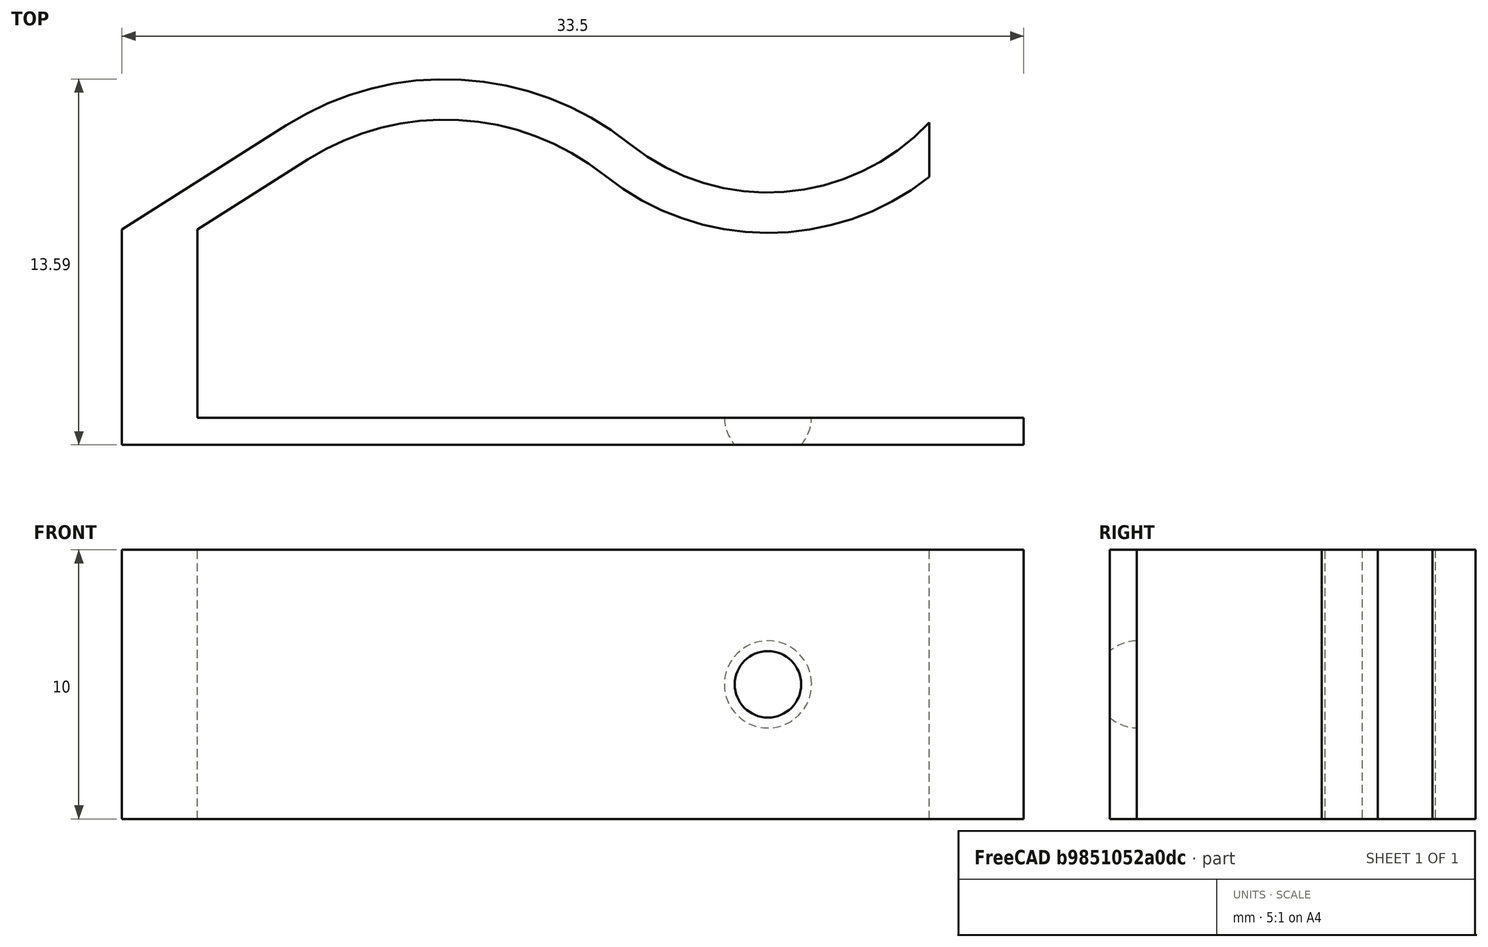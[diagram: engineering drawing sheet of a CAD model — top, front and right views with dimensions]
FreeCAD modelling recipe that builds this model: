
FCSTD DOCUMENT  (FreeCAD 0.16R5342 (Git))
Label: BluRayLensHolder
License: All rights reserved
LicenseURL: http://en.wikipedia.org/wiki/All_rights_reserved
objects: Sketcher::SketchObject×2, Mesh::Feature×1, App::DocumentObjectGroup×1, PartDesign::Pad×1, Part::Revolution×1, Part::Cut×1
note: 6 computed .brp shape members not serialized (recipe doc carries the construction recipe); baked Part::Feature solids carry a one-line shape summary decoded from their .brp

FEATURE [Mesh::Feature] _50Clip  label="350Clip"
  Placement = pos=(0,-2,0) rot=(0,0,1;0rad)
FEATURE [App::DocumentObjectGroup] Group  label="Reference"
  Group = -> [_50Clip]
FEATURE [Sketcher::SketchObject] Sketch  label="Base"
  sketch-geometry (14):
    g0: LineSegment StartX=0 StartY=8 StartZ=0 EndX=0 EndY=0 EndZ=0
    g1: LineSegment StartX=0 StartY=0 StartZ=0 EndX=33.5 EndY=0 EndZ=0
    g2: LineSegment StartX=33.5 StartY=0 StartZ=0 EndX=33.5 EndY=1 EndZ=0
    g3: LineSegment StartX=33.5 StartY=1 StartZ=0 EndX=2.8 EndY=1 EndZ=0
    g4: LineSegment StartX=2.8 StartY=1 StartZ=0 EndX=2.8 EndY=8 EndZ=0
    g5: LineSegment StartX=0 StartY=8 StartZ=0 EndX=6.10713 EndY=11.8746 EndZ=0
    g6: LineSegment StartX=2.8 StartY=8 StartZ=0 EndX=6.91071 EndY=10.608 EndZ=0
    g7: ArcOfCircle CenterX=12 CenterY=2.58618 CenterZ=0 NormalX=0 NormalY=0 NormalZ=1 Radius=11 StartAngle=0.896055 EndAngle=2.13615
    g8: ArcOfCircle CenterX=12 CenterY=2.58618 CenterZ=0 NormalX=0 NormalY=0 NormalZ=1 Radius=9.5 StartAngle=0.896055 EndAngle=2.13615
    g9: ArcOfCircle CenterX=24 CenterY=17.5862 CenterZ=0 NormalX=0 NormalY=0 NormalZ=1 Radius=9.70937 StartAngle=4.03765 EndAngle=5.37853
    g10: ArcOfCircle CenterX=24 CenterY=17.5862 CenterZ=0 NormalX=0 NormalY=0 NormalZ=1 Radius=8.20937 StartAngle=4.03765 EndAngle=5.53199
    g11: LineSegment StartX=30 StartY=11.9832 StartZ=0 EndX=30 EndY=9.95257 EndZ=0
    g12: LineSegment [constr] StartX=6.10713 StartY=11.8746 StartZ=0 EndX=6.91071 EndY=10.608 EndZ=0
    g13: LineSegment [constr] StartX=18.8716 StartY=11.1757 StartZ=0 EndX=17.9346 EndY=10.0044 EndZ=0
  constraints (42):
    c: Coincident(g0,g1)
    c: Coincident(g1,g2)
    c: Coincident(g2,g3)
    c: Coincident(g3,g4)
    c: Coincident(g0,g5)
    c: Coincident(g4,g6)
    c: Coincident(g7,g5)
    c: Coincident(g6,g8)
    c: Coincident(g8,g9)
    c: Coincident(g7,g10)
    c: Coincident(g9,g11)
    c: Coincident(g10,g11)
    c: Horizontal(g3)
    c: Horizontal(g1)
    c: Vertical(g2)
    c: Vertical(g4)
    c: Vertical(g0)
    c: Tangent(g7,g5)
    c: Tangent(g6,g8)
    c: Tangent(g7,g10)
    c: Tangent(g8,g9)
    c: Parallel(g6,g5)
    c: Coincident(g7,g8)
    c: Coincident(g9,g10)
    c: Vertical(g11)
    c: Coincident(g0,g-1)
    c: DistanceY(g2) = 1
    c: DistanceX(g1) = 33.5
    c: DistanceX(g0,g4) = 2.8
    c: DistanceY(g0) = 8
    c: DistanceY(g4,g0) = 0
    c: DistanceX(g9) = 30
    c: Coincident(g12,g6)
    c: Coincident(g12,g5)
    c: Coincident(g13,g8)
    c: Coincident(g13,g7)
    c: Equal(g12,g13)
    c: Distance(g12) = 1.5
    c: DistanceX(g7) = 12
    c: DistanceX(g7,g9) = 12
    c: DistanceY(g9,g7) = -15
    c: Radius(g7) = 11
FEATURE [PartDesign::Pad] Pad  label="Base001"
  Length = 10
  Length2 = 100
  Sketch = -> Sketch
  Type = 0
FEATURE [Sketcher::SketchObject] Sketch001  label="Sphere"
  sketch-geometry (3):
    g0: ArcOfCircle CenterX=0 CenterY=-0.0507962 CenterZ=0 NormalX=0 NormalY=0 NormalZ=1 Radius=1.6208 StartAngle=1.5708 EndAngle=3.11025
    g1: LineSegment StartX=0 StartY=1.57 StartZ=0 EndX=0 EndY=0 EndZ=0
    g2: LineSegment StartX=0 StartY=0 StartZ=0 EndX=-1.62 EndY=0 EndZ=0
  constraints (10):
    c: PointOnObject(g0,g-1)
    c: PointOnObject(g0,g-2)
    c: Coincident(g2,g0)
    c: Coincident(g2,g-1)
    c: Coincident(g1,g-1)
    c: Coincident(g1,g0)
    c: DistanceY(g1) = -1.57
    c: DistanceX(g2) = -1.62
    c: PointOnObject(g0,g-2)
    c: Radius(g0) = 1.6208
FEATURE [Part::Revolution] Revolve  label="Spherecut"
  Angle = 360
  Axis = (0,1,0)
  Base = (0,0,0)
  Placement = pos=(24,1,5) rot=(0,0,1;3.14159rad)
  Solid = true
  Source = -> Sketch001
FEATURE [Part::Cut] Cut  label="SphereCut"
  Base = -> Pad
  Tool = -> Revolve
